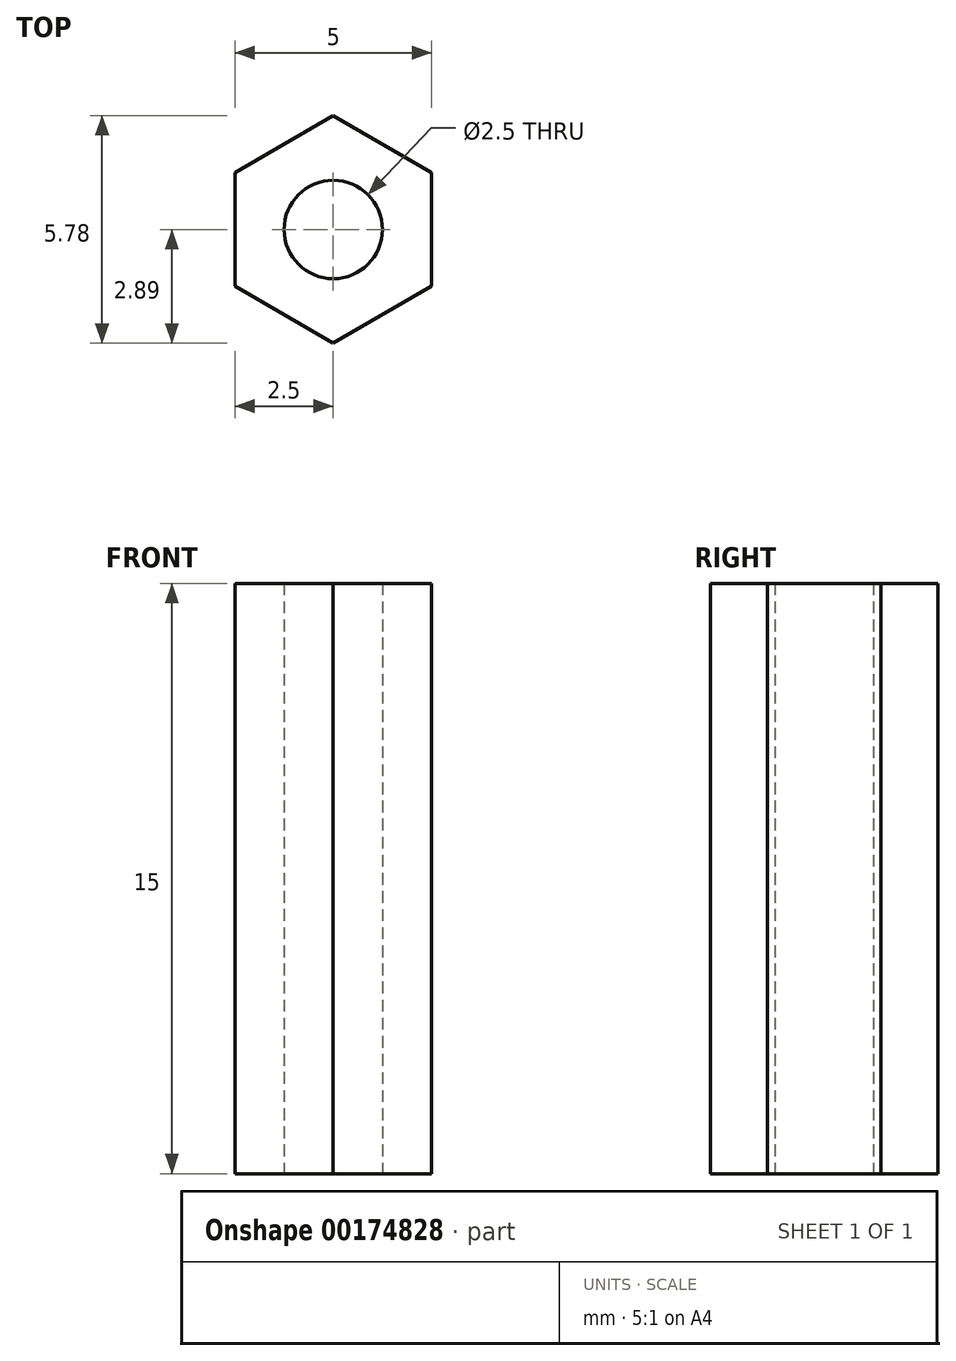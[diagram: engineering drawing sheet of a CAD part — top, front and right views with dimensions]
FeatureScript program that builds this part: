
annotation { "Feature Type Name" : "Feature", "Feature Type Description" : "" }
export const myFeature = defineFeature(function(context is Context, id is Id, definition is map)
    precondition{}
    {
        {
            var Q0;
            Q0=qCreatedBy(makeId("Top.planeOp"),FACE);
            var sketch = newSketch(context, id + "F0", { "sketchPlane" : qUnion([Q0])});
            skCircle(sketch, "E0.cCircle", {"center": v(0, 0) * mm, "radius": 2.5 * mm, "construction": true});
            skLineSegment(sketch, "E0.0", {"start": v(2.5, -1.44) * mm, "end": v(0, -2.89) * mm});
            skLineSegment(sketch, "E0.1", {"start": v(0, -2.89) * mm, "end": v(-2.5, -1.44) * mm});
            skLineSegment(sketch, "E0.2", {"start": v(-2.5, -1.44) * mm, "end": v(-2.5, 1.44) * mm});
            skLineSegment(sketch, "E0.3", {"start": v(-2.5, 1.44) * mm, "end": v(0, 2.89) * mm});
            skLineSegment(sketch, "E0.4", {"start": v(0, 2.89) * mm, "end": v(2.5, 1.44) * mm});
            skLineSegment(sketch, "E0.5", {"start": v(2.5, 1.44) * mm, "end": v(2.5, -1.44) * mm});
            skPoint(sketch, "E0.0.midPoint", {"position": v(1.25, -2.17) * mm});
            skCircle(sketch, "E1", {"center": v(0, 0) * mm, "radius": 1.25 * mm});
            skSolve(sketch);
        }
        {
            var Q0;
            Q0=qSketchRegion(id+"F0",true);
            extrude(context, id + "F1", {"entities" : qUnion([Q0]), "depth" : 15 * mm});
        }
    });
